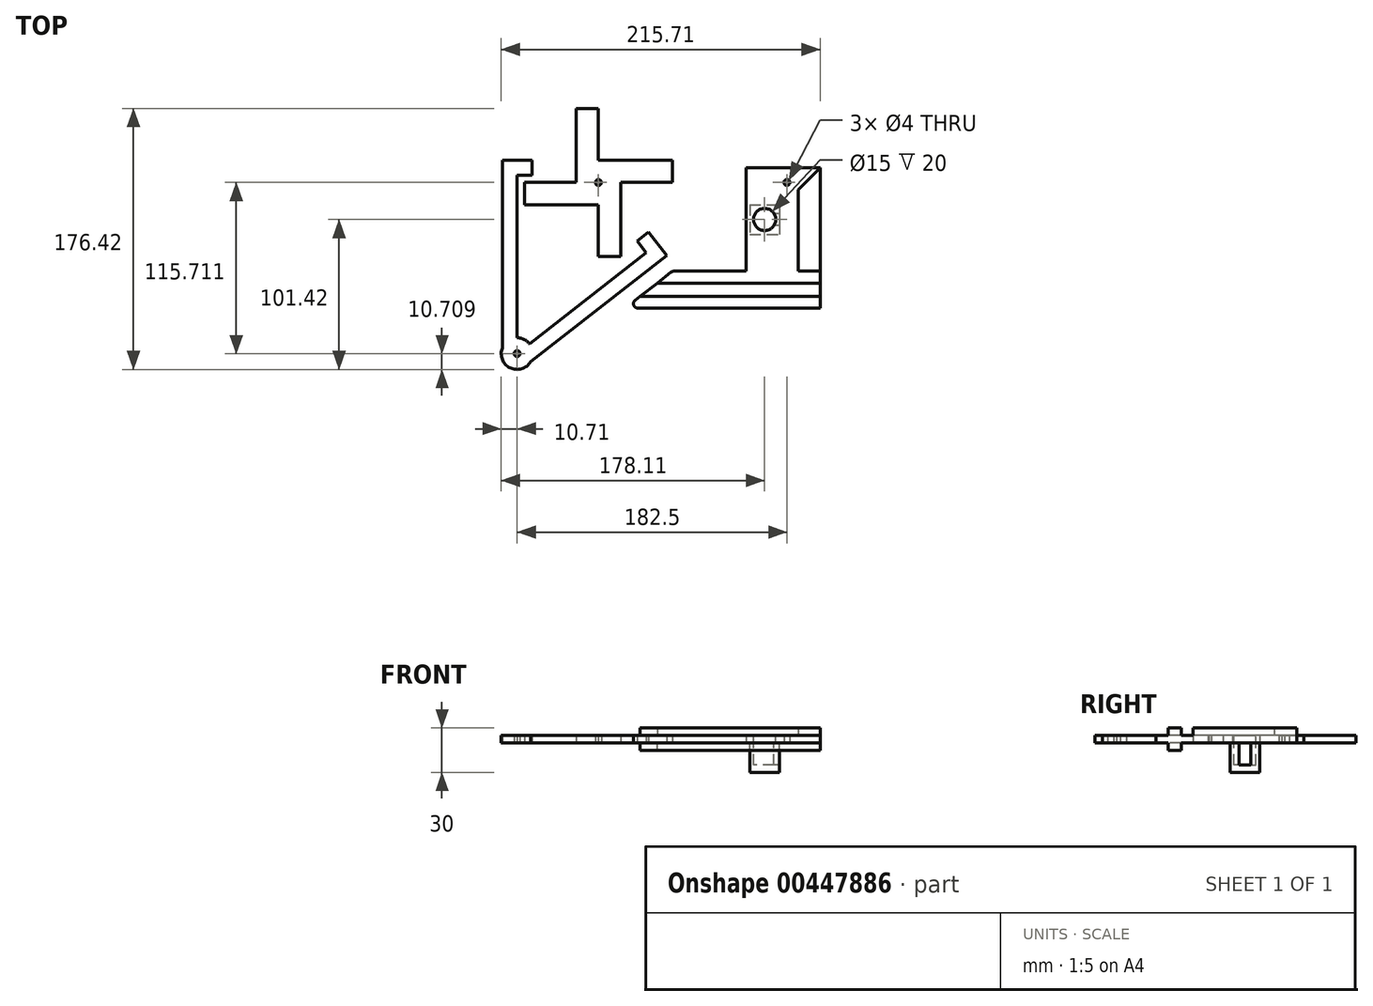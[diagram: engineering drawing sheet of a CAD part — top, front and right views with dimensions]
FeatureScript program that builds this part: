
annotation { "Feature Type Name" : "Feature", "Feature Type Description" : "" }
export const myFeature = defineFeature(function(context is Context, id is Id, definition is map)
    precondition{}
    {
        {
            var Q0;
            Q0=qCreatedBy(makeId("Top.planeOp"),FACE);
            var sketch = newSketch(context, id + "F0", { "sketchPlane" : qUnion([Q0])});
            skPoint(sketch, "E0.middle", {"position": v(0, 0) * mm});
            skLineSegment(sketch, "E1.bottom", {"start": v(0, 0) * mm, "end": v(15, 0) * mm});
            skLineSegment(sketch, "E1.top", {"start": v(0, -50) * mm, "end": v(15, -50) * mm});
            skLineSegment(sketch, "E1.left", {"start": v(0, 0) * mm, "end": v(0, -50) * mm});
            skLineSegment(sketch, "E1.right", {"start": v(15, 0) * mm, "end": v(15, -50) * mm});
            skLineSegment(sketch, "E2.bottom", {"start": v(0, 0) * mm, "end": v(-50, 0) * mm});
            skLineSegment(sketch, "E2.top", {"start": v(0, -15) * mm, "end": v(-50, -15) * mm});
            skLineSegment(sketch, "E2.left", {"start": v(0, 0) * mm, "end": v(0, -15) * mm});
            skLineSegment(sketch, "E2.right", {"start": v(-50, 0) * mm, "end": v(-50, -15) * mm});
            skLineSegment(sketch, "E3.bottom", {"start": v(0, 0) * mm, "end": v(-15, 0) * mm});
            skLineSegment(sketch, "E3.top", {"start": v(0, 50) * mm, "end": v(-15, 50) * mm});
            skLineSegment(sketch, "E3.left", {"start": v(0, 0) * mm, "end": v(0, 50) * mm});
            skLineSegment(sketch, "E3.right", {"start": v(-15, 0) * mm, "end": v(-15, 50) * mm});
            skLineSegment(sketch, "E4.bottom", {"start": v(0, 0) * mm, "end": v(50, 0) * mm});
            skLineSegment(sketch, "E4.top", {"start": v(0, 15) * mm, "end": v(50, 15) * mm});
            skLineSegment(sketch, "E4.left", {"start": v(0, 0) * mm, "end": v(0, 15) * mm});
            skLineSegment(sketch, "E4.right", {"start": v(50, 0) * mm, "end": v(50, 15) * mm});
            skCircle(sketch, "E5", {"center": v(0, 0) * mm, "radius": 2 * mm});
            skSolve(sketch);
        }
        {
            var Q0;
            Q0 = qSketchRegion(id + "F0", true);
            extrude(context, id + "F1", {"entities" : qUnion([Q0]), "depth" : 5 * mm});
        }
        {
            var Q0;
            Q0=qCreatedBy(makeId("Top.planeOp"),FACE);
            var sketch = newSketch(context, id + "F2", { "sketchPlane" : qUnion([Q0])});
            skLineSegment(sketch, "E6", {"start": v(-55, 5) * mm, "end": v(-45, 5) * mm});
            skLineSegment(sketch, "E7", {"start": v(-45, 5) * mm, "end": v(-45, 15) * mm});
            skLineSegment(sketch, "E8", {"start": v(-45, 15) * mm, "end": v(-65, 15) * mm});
            skLineSegment(sketch, "E9", {"start": v(40.12, -41.4) * mm, "end": v(33.96, -33.51) * mm});
            skLineSegment(sketch, "E10", {"start": v(33.96, -33.51) * mm, "end": v(26.08, -39.67) * mm});
            skLineSegment(sketch, "E11", {"start": v(26.08, -39.67) * mm, "end": v(32.24, -47.55) * mm});
            skLineSegment(sketch, "E12", {"start": v(40.12, -41.4) * mm, "end": v(46.28, -49.27) * mm});
            skPoint(sketch, "E13", {"position": v(-55, -115.71) * mm});
            skCircle(sketch, "E14", {"center": v(-55, -115.71) * mm, "radius": 10.71 * mm});
            skLineSegment(sketch, "E15", {"start": v(32.24, -47.55) * mm, "end": v(-46.56, -109.12) * mm});
            skLineSegment(sketch, "E16", {"start": v(46.28, -49.27) * mm, "end": v(-45.82, -121.23) * mm});
            skCircle(sketch, "E17", {"center": v(-55, -115.71) * mm, "radius": 2 * mm});
            skLineSegment(sketch, "E18", {"start": v(-65, 15) * mm, "end": v(-65, -111.87) * mm});
            skLineSegment(sketch, "E19", {"start": v(-55, 5) * mm, "end": v(-55, -105) * mm});
            skSolve(sketch);
        }
        {
            var Q0;
            Q0=qCreatedBy(makeId("Top.planeOp"),FACE);
            var sketch = newSketch(context, id + "F3", { "sketchPlane" : qUnion([Q0])});
            skLineSegment(sketch, "E20", {"start": v(100, 10) * mm, "end": v(100, -60) * mm});
            skLineSegment(sketch, "E21", {"start": v(100, -60) * mm, "end": v(51.03, -60) * mm});
            skLineSegment(sketch, "E22", {"start": v(49.19, -60.64) * mm, "end": v(24.87, -79.64) * mm});
            skPoint(sketch, "E23.visualSharp", {"position": v(18, -85) * mm});
            skArc(sketch, "E23.filletArc", {"start": v(24.87, -79.64) * mm, "mid": v(23.88, -82.98) * mm, "end": v(26.71, -85) * mm});
            skPoint(sketch, "E24.visualSharp", {"position": v(50, -60) * mm});
            skArc(sketch, "E24.filletArc", {"start": v(51.03, -60) * mm, "mid": v(50.06, -60.16) * mm, "end": v(49.19, -60.64) * mm});
            skLineSegment(sketch, "E25", {"start": v(100, 10) * mm, "end": v(150, 10) * mm});
            skPoint(sketch, "E26", {"position": v(127.5, 0) * mm});
            skCircle(sketch, "E27", {"center": v(127.5, 0) * mm, "radius": 2 * mm});
            skLineSegment(sketch, "E28", {"start": v(150, 10) * mm, "end": v(150, -85) * mm});
            skLineSegment(sketch, "E29", {"start": v(26.71, -85) * mm, "end": v(150, -85) * mm});
            skSolve(sketch);
        }
        {
            var Q0;
            Q0 = qSketchRegion(id + "F3", true);
            extrude(context, id + "F4", {"entities" : qUnion([Q0]), "depth" : 5 * mm});
        }
        {
            var Q0;
            Q0=makeQuery(id+"F4.opExtrude","CAP_FACE",FACE,{"disambiguationData":[OSD([sQuery(id+"F3.wireOp",EDGE,"E20"),sQuery(id+"F3.wireOp",EDGE,"E21"),sQuery(id+"F3.wireOp",EDGE,"E22"),sQuery(id+"F3.wireOp",EDGE,"E23.filletArc"),sQuery(id+"F3.wireOp",EDGE,"E24.filletArc"),sQuery(id+"F3.wireOp",EDGE,"E25"),sQuery(id+"F3.wireOp",EDGE,"E27"),sQuery(id+"F3.wireOp",EDGE,"E28"),sQuery(id+"F3.wireOp",EDGE,"E29")])],"isStart":false});
            var sketch = newSketch(context, id + "F5", { "sketchPlane" : qUnion([Q0])});
            skLineSegment(sketch, "E30", {"start": v(150, 10) * mm, "end": v(135, -5) * mm});
            skLineSegment(sketch, "E31", {"start": v(135, -5) * mm, "end": v(135, -60) * mm});
            skLineSegment(sketch, "E32", {"start": v(135, -60) * mm, "end": v(150, -60) * mm});
            skLineSegment(sketch, "E33", {"start": v(150, -60) * mm, "end": v(150, 10) * mm});
            skSolve(sketch);
        }
        {
            var Q0;
            Q0 = qSketchRegion(id + "F5", true);
            extrude(context, id + "F6", {"entities" : qUnion([Q0]), "operationType" : NewBodyOperationType.ADD, "depth" : 5 * mm});
        }
        {
            var Q0;
            Q0=makeQuery(id+"F4.opExtrude","CAP_FACE",FACE,{"disambiguationData":[OSD([sQuery(id+"F3.wireOp",EDGE,"E20"),sQuery(id+"F3.wireOp",EDGE,"E21"),sQuery(id+"F3.wireOp",EDGE,"E22"),sQuery(id+"F3.wireOp",EDGE,"E23.filletArc"),sQuery(id+"F3.wireOp",EDGE,"E24.filletArc"),sQuery(id+"F3.wireOp",EDGE,"E25"),sQuery(id+"F3.wireOp",EDGE,"E27"),sQuery(id+"F3.wireOp",EDGE,"E28"),sQuery(id+"F3.wireOp",EDGE,"E29")])],"isStart":false});
            var sketch = newSketch(context, id + "F7", { "sketchPlane" : qUnion([Q0])});
            skPoint(sketch, "E34", {"position": v(112.4, -25) * mm});
            skCircle(sketch, "E35", {"center": v(112.4, -25) * mm, "radius": 7.5 * mm});
            skSolve(sketch);
        }
        {
            var Q0;
            Q0 = qSketchRegion(id + "F7", true);
            extrude(context, id + "F8", {"entities" : qUnion([Q0]), "operationType" : NewBodyOperationType.REMOVE, "endBound" : BoundingType.THROUGH_ALL, "oppositeDirection" : true, "depth" : 25 * mm});
        }
        {
            var Q0;
            Q0=makeQuery(id+"F4.opExtrude","CAP_FACE",FACE,{"disambiguationData":[OSD([sQuery(id+"F3.wireOp",EDGE,"E20"),sQuery(id+"F3.wireOp",EDGE,"E21"),sQuery(id+"F3.wireOp",EDGE,"E22"),sQuery(id+"F3.wireOp",EDGE,"E23.filletArc"),sQuery(id+"F3.wireOp",EDGE,"E24.filletArc"),sQuery(id+"F3.wireOp",EDGE,"E25"),sQuery(id+"F3.wireOp",EDGE,"E27"),sQuery(id+"F3.wireOp",EDGE,"E28"),sQuery(id+"F3.wireOp",EDGE,"E29")])],"isStart":false});
            var sketch = newSketch(context, id + "F9", { "sketchPlane" : qUnion([Q0])});
            skLineSegment(sketch, "E36", {"start": v(150, -77) * mm, "end": v(28.24, -77) * mm});
            skLineSegment(sketch, "E37", {"start": v(150, -68) * mm, "end": v(39.76, -68) * mm});
            skLineSegment(sketch, "E38", {"start": v(28.24, -77) * mm, "end": v(39.76, -68) * mm});
            skLineSegment(sketch, "E39", {"start": v(150, -68) * mm, "end": v(150, -77) * mm});
            skSolve(sketch);
        }
        {
            var Q0;
            Q0 = qSketchRegion(id + "F9", true);
            extrude(context, id + "F10", {"entities" : qUnion([Q0]), "operationType" : NewBodyOperationType.ADD, "depth" : 5 * mm});
        }
        {
            var Q0;
            Q0=makeQuery(id+"F4.opExtrude","CAP_FACE",FACE,{"disambiguationData":[OSD([sQuery(id+"F3.wireOp",EDGE,"E20"),sQuery(id+"F3.wireOp",EDGE,"E21"),sQuery(id+"F3.wireOp",EDGE,"E22"),sQuery(id+"F3.wireOp",EDGE,"E23.filletArc"),sQuery(id+"F3.wireOp",EDGE,"E24.filletArc"),sQuery(id+"F3.wireOp",EDGE,"E25"),sQuery(id+"F3.wireOp",EDGE,"E27"),sQuery(id+"F3.wireOp",EDGE,"E28"),sQuery(id+"F3.wireOp",EDGE,"E29")])],"isStart":true});
            var sketch = newSketch(context, id + "F11", { "sketchPlane" : qUnion([Q0])});
            skLineSegment(sketch, "E40", {"start": v(150, 77) * mm, "end": v(28.24, 77) * mm});
            skLineSegment(sketch, "E41", {"start": v(28.24, 77) * mm, "end": v(39.76, 68) * mm});
            skLineSegment(sketch, "E42", {"start": v(39.76, 68) * mm, "end": v(150, 68) * mm});
            skLineSegment(sketch, "E43", {"start": v(150, 68) * mm, "end": v(150, 77) * mm});
            skSolve(sketch);
        }
        {
            var Q0;
            Q0 = qSketchRegion(id + "F11", true);
            extrude(context, id + "F12", {"entities" : qUnion([Q0]), "operationType" : NewBodyOperationType.ADD, "depth" : 5 * mm});
        }
        {
            var Q0;
            Q0 = qSketchRegion(id + "F2", true);
            extrude(context, id + "F13", {"entities" : qUnion([Q0]), "depth" : 5 * mm});
        }
        {
            var Q0;
            {var subQ0=sQuery(id+"F3.wireOp",EDGE,"E21");var subQ1=sQuery(id+"F3.wireOp",EDGE,"E28");var subQ2=sQuery(id+"F3.wireOp",EDGE,"E27");var subQ3=sQuery(id+"F3.wireOp",EDGE,"E25");var subQ4=sQuery(id+"F3.wireOp",EDGE,"E20");var subQ5=sQuery(id+"F3.wireOp",EDGE,"E22");var subQ6=sQuery(id+"F3.wireOp",EDGE,"E24.filletArc");Q0=makeQuery(id+"F12.boolean.opBoolean","SPLIT",FACE,{"disambiguationData":[TD([makeQuery(id+"F4.opExtrude","SWEPT_FACE",FACE,{"disambiguationData":[OSD([subQ4])]})])],"derivedFrom":makeQuery(id+"F4.opExtrude","CAP_FACE",FACE,{"disambiguationData":[OSD([subQ4,subQ0,subQ5,sQuery(id+"F3.wireOp",EDGE,"E23.filletArc"),subQ6,subQ3,subQ2,subQ1,sQuery(id+"F3.wireOp",EDGE,"E29")])],"isStart":true})});}
            var sketch = newSketch(context, id + "F14", { "sketchPlane" : qUnion([Q0])});
            skPoint(sketch, "E44", {"position": v(112.4, 25) * mm});
            skLineSegment(sketch, "E45.bottom", {"start": v(102.4, 15) * mm, "end": v(122.4, 15) * mm});
            skLineSegment(sketch, "E45.top", {"start": v(102.4, 35) * mm, "end": v(122.4, 35) * mm});
            skLineSegment(sketch, "E45.left", {"start": v(102.4, 15) * mm, "end": v(102.4, 35) * mm});
            skPoint(sketch, "E46", {"position": v(122.4, 21) * mm});
            skPoint(sketch, "E47", {"position": v(122.4, 29) * mm});
            skLineSegment(sketch, "E48", {"start": v(122.4, 21) * mm, "end": v(118.74, 21) * mm});
            skLineSegment(sketch, "E49", {"start": v(122.4, 29) * mm, "end": v(118.74, 29) * mm});
            skLineSegment(sketch, "E50", {"start": v(122.4, 15) * mm, "end": v(122.4, 21) * mm});
            skLineSegment(sketch, "E51", {"start": v(122.4, 29) * mm, "end": v(122.4, 35) * mm});
            skArc(sketch, "E52", {"start": v(118.74, 21) * mm, "mid": v(104.9, 25) * mm, "end": v(118.74, 29) * mm});
            skSolve(sketch);
        }
        {
            var Q0;
            Q0 = qSketchRegion(id + "F14", true);
            extrude(context, id + "F15", {"entities" : qUnion([Q0]), "operationType" : NewBodyOperationType.ADD, "depth" : 15 * mm});
        }
        {
            var Q0;
            Q0=makeQuery(id+"F15.opExtrude","CAP_FACE",FACE,{"disambiguationData":[OSD([sQuery(id+"F14.wireOp",EDGE,"E45.bottom"),sQuery(id+"F14.wireOp",EDGE,"E45.top"),sQuery(id+"F14.wireOp",EDGE,"E45.left"),sQuery(id+"F14.wireOp",EDGE,"E48"),sQuery(id+"F14.wireOp",EDGE,"E49"),sQuery(id+"F14.wireOp",EDGE,"E50"),sQuery(id+"F14.wireOp",EDGE,"E51"),sQuery(id+"F14.wireOp",EDGE,"E52")])],"isStart":false});
            var sketch = newSketch(context, id + "F16", { "sketchPlane" : qUnion([Q0])});
            skLineSegment(sketch, "E53.bottom", {"start": v(102.4, 15) * mm, "end": v(122.4, 15) * mm});
            skLineSegment(sketch, "E53.top", {"start": v(102.4, 35) * mm, "end": v(122.4, 35) * mm});
            skLineSegment(sketch, "E53.left", {"start": v(102.4, 15) * mm, "end": v(102.4, 35) * mm});
            skLineSegment(sketch, "E53.right", {"start": v(122.4, 15) * mm, "end": v(122.4, 35) * mm});
            skSolve(sketch);
        }
        {
            var Q0;
            Q0 = qSketchRegion(id + "F16", true);
            extrude(context, id + "F17", {"entities" : qUnion([Q0]), "operationType" : NewBodyOperationType.ADD, "depth" : 5 * mm});
        }
    });
